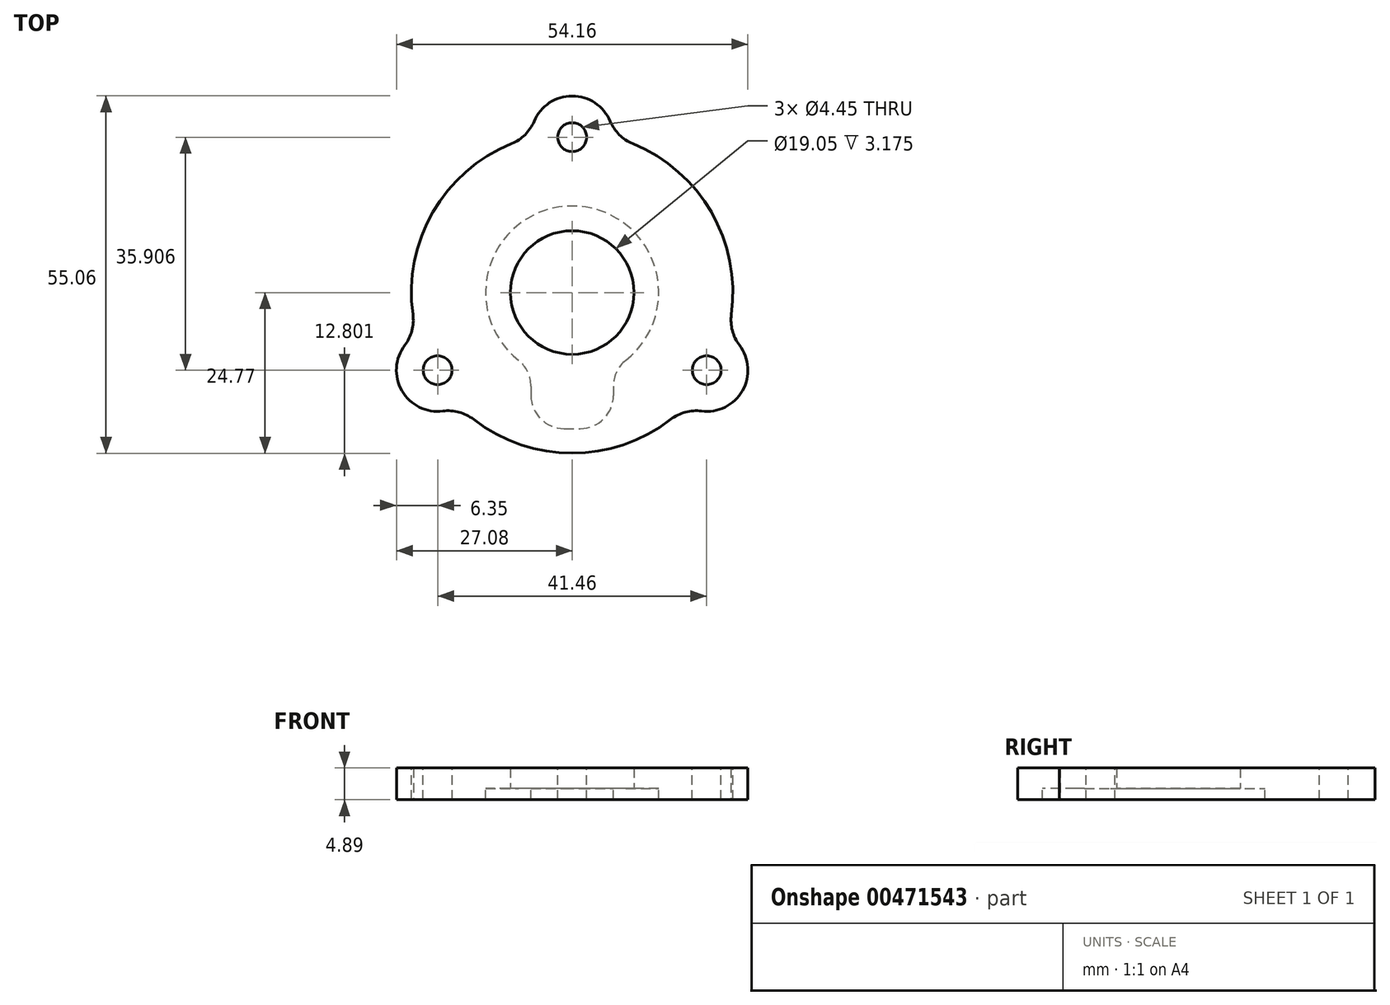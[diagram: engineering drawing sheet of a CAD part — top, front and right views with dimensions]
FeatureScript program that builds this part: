
annotation { "Feature Type Name" : "Feature", "Feature Type Description" : "" }
export const myFeature = defineFeature(function(context is Context, id is Id, definition is map)
    precondition{}
    {
        {
            var Q0;
            Q0=qCreatedBy(makeId("Top.planeOp"),FACE);
            var sketch = newSketch(context, id + "F0", { "sketchPlane" : qUnion([Q0])});
            skCircle(sketch, "E0", {"center": v(0, 0) * mm, "radius": 24.77 * mm});
            skLineSegment(sketch, "E1", {"start": v(0, 0) * mm, "end": v(0, 42.77) * mm, "construction": true});
            skLineSegment(sketch, "E2", {"start": v(0, 0) * mm, "end": v(-43.71, -25.24) * mm, "construction": true});
            skLineSegment(sketch, "E3", {"start": v(0, 0) * mm, "end": v(46.9, -27.08) * mm, "construction": true});
            skLineSegment(sketch, "E4", {"start": v(-6.35, 2.16) * mm, "end": v(-6.35, 48.97) * mm, "construction": true});
            skLineSegment(sketch, "E5.MirrorCS", {"start": v(6.35, 2.16) * mm, "end": v(6.35, 48.97) * mm, "construction": true});
            skLineSegment(sketch, "E6", {"start": v(-12.7, 0) * mm, "end": v(-48.99, -20.95) * mm, "construction": true});
            skLineSegment(sketch, "E7.MirrorCS", {"start": v(-6.35, -11) * mm, "end": v(-42.64, -31.95) * mm, "construction": true});
            skLineSegment(sketch, "E8", {"start": v(0.14, -7.41) * mm, "end": v(38.48, -29.55) * mm, "construction": true});
            skLineSegment(sketch, "E9.MirrorCS", {"start": v(6.49, 3.59) * mm, "end": v(44.83, -18.55) * mm, "construction": true});
            skArc(sketch, "E10", {"start": v(6.35, 23.94) * mm, "mid": v(0, 30.29) * mm, "end": v(-6.35, 23.94) * mm});
            skArc(sketch, "E11", {"start": v(-23.9, -6.47) * mm, "mid": v(-26.23, -15.14) * mm, "end": v(-17.56, -17.47) * mm});
            skArc(sketch, "E12", {"start": v(17.56, -17.47) * mm, "mid": v(26.23, -15.14) * mm, "end": v(23.9, -6.47) * mm});
            skCircle(sketch, "E13", {"center": v(0, 23.94) * mm, "radius": 2.22 * mm});
            skCircle(sketch, "E14", {"center": v(-20.73, -11.97) * mm, "radius": 2.22 * mm});
            skCircle(sketch, "E15", {"center": v(20.73, -11.97) * mm, "radius": 2.22 * mm});
            skCircle(sketch, "E16", {"center": v(0, 0) * mm, "radius": 9.53 * mm});
            skCircle(sketch, "E17", {"center": v(0, 0) * mm, "radius": 13.34 * mm});
            skLineSegment(sketch, "E18", {"start": v(-6.35, -11.73) * mm, "end": v(-6.35, -20.96) * mm});
            skLineSegment(sketch, "E19.MirrorCS", {"start": v(6.35, -11.73) * mm, "end": v(6.35, -20.96) * mm});
            skLineSegment(sketch, "E20", {"start": v(-6.35, -20.96) * mm, "end": v(6.35, -20.96) * mm});
            skSolve(sketch);
        }
        {
            var Q0;
            Q0 = qSketchRegion(id + "F0", true);
            extrude(context, id + "F1", {"entities" : qUnion([Q0]), "oppositeDirection" : true, "depth" : 1.71 * mm});
        }
        {
            var Q0;
            Q0=makeQuery(id+"F0.imprint","IMPRINT",FACE,{"disambiguationData":[TD([[makeQuery(id+"F0.imprint","IMPRINT",EDGE,{"derivedFrom":sQuery(id+"F0.wireOp",EDGE,"E16")}),-1.0]])]});
            var Q1;
            Q1=makeQuery(id+"F0.imprint","IMPRINT",FACE,{"disambiguationData":[TD([[makeQuery(id+"F0.imprint","IMPRINT",EDGE,{"derivedFrom":sQuery(id+"F0.wireOp",EDGE,"E17")}),-1.0]])]});
            var Q2;
            {var subQ0=sQuery(id+"F0.wireOp",EDGE,"E10");Q2=makeQuery(id+"F0.imprint","IMPRINT",FACE,{"disambiguationData":[TD([[makeQuery(id+"F0.imprint","IMPRINT",EDGE,{"derivedFrom":subQ0}),1.0]])]});}
            var Q3;
            {var subQ0=sQuery(id+"F0.wireOp",EDGE,"E11");Q3=makeQuery(id+"F0.imprint","IMPRINT",FACE,{"disambiguationData":[TD([[makeQuery(id+"F0.imprint","IMPRINT",EDGE,{"derivedFrom":subQ0}),1.0]])]});}
            var Q4;
            {var subQ0=sQuery(id+"F0.wireOp",EDGE,"E12");Q4=makeQuery(id+"F0.imprint","IMPRINT",FACE,{"disambiguationData":[TD([[makeQuery(id+"F0.imprint","IMPRINT",EDGE,{"derivedFrom":subQ0}),1.0]])]});}
            var Q5;
            {var subQ16=sQuery(id+"F0.wireOp",EDGE,"E18");Q5=makeQuery(id+"F0.imprint","IMPRINT",FACE,{"disambiguationData":[TD([[makeQuery(id+"F0.imprint","IMPRINT",EDGE,{"derivedFrom":subQ16}),-1.0]])]});}
            extrude(context, id + "F2", {"entities" : qUnion([Q0, Q1, Q2, Q3, Q4, Q5]), "operationType" : NewBodyOperationType.ADD, "depth" : 3.17 * mm});
        }
        {
            var Q0;
            {var subQ0=sQuery(id+"F0.wireOp",EDGE,"E11");var subQ1=sQuery(id+"F0.wireOp",EDGE,"E0");Q0=makeQuery(id+"F1.opExtrude","SWEPT_EDGE",EDGE,{"disambiguationData":[OSD([subQ1,subQ0]),TDD([makeQuery(id+"F0.imprint","INTERSECT",VERTEX,{"disambiguationData":[OD(1.0)],"derivedFrom":[subQ1,subQ0]})])]});}
            var Q1;
            {var subQ0=sQuery(id+"F0.wireOp",EDGE,"E11");var subQ1=sQuery(id+"F0.wireOp",EDGE,"E0");Q1=makeQuery(id+"F1.opExtrude","SWEPT_EDGE",EDGE,{"disambiguationData":[OSD([subQ1,subQ0]),TDD([makeQuery(id+"F0.imprint","INTERSECT",VERTEX,{"disambiguationData":[OD(0.0)],"derivedFrom":[subQ1,subQ0]})])]});}
            var Q2;
            {var subQ0=sQuery(id+"F0.wireOp",EDGE,"E10");var subQ1=sQuery(id+"F0.wireOp",EDGE,"E0");Q2=makeQuery(id+"F1.opExtrude","SWEPT_EDGE",EDGE,{"disambiguationData":[OSD([subQ1,subQ0]),TDD([makeQuery(id+"F0.imprint","INTERSECT",VERTEX,{"disambiguationData":[OD(1.0)],"derivedFrom":[subQ1,subQ0]})])]});}
            var Q3;
            {var subQ0=sQuery(id+"F0.wireOp",EDGE,"E10");var subQ1=sQuery(id+"F0.wireOp",EDGE,"E0");Q3=makeQuery(id+"F1.opExtrude","SWEPT_EDGE",EDGE,{"disambiguationData":[OSD([subQ1,subQ0]),TDD([makeQuery(id+"F0.imprint","INTERSECT",VERTEX,{"disambiguationData":[OD(0.0)],"derivedFrom":[subQ1,subQ0]})])]});}
            var Q4;
            {var subQ0=sQuery(id+"F0.wireOp",EDGE,"E12");var subQ1=sQuery(id+"F0.wireOp",EDGE,"E0");Q4=makeQuery(id+"F1.opExtrude","SWEPT_EDGE",EDGE,{"disambiguationData":[OSD([subQ1,subQ0]),TDD([makeQuery(id+"F0.imprint","INTERSECT",VERTEX,{"disambiguationData":[OD(1.0)],"derivedFrom":[subQ1,subQ0]})])]});}
            var Q5;
            {var subQ0=sQuery(id+"F0.wireOp",EDGE,"E12");var subQ1=sQuery(id+"F0.wireOp",EDGE,"E0");Q5=makeQuery(id+"F1.opExtrude","SWEPT_EDGE",EDGE,{"disambiguationData":[OSD([subQ1,subQ0]),TDD([makeQuery(id+"F0.imprint","INTERSECT",VERTEX,{"disambiguationData":[OD(0.0)],"derivedFrom":[subQ1,subQ0]})])]});}
            fillet(context, id + "F3", {"entities" : qUnion([Q0, Q1, Q2, Q3, Q4, Q5]), "radius" : 6.35 * mm, "tangentPropagation" : true, "allowEdgeOverflow" : false});
        }
        {
            var Q0;
            Q0=makeQuery(id+"F1.opExtrude","SWEPT_EDGE",EDGE,{"disambiguationData":[OSD([sQuery(id+"F0.wireOp",EDGE,"E17"),sQuery(id+"F0.wireOp",EDGE,"E18")])]});
            var Q1;
            Q1=makeQuery(id+"F1.opExtrude","SWEPT_EDGE",EDGE,{"disambiguationData":[OSD([sQuery(id+"F0.wireOp",EDGE,"E17"),sQuery(id+"F0.wireOp",EDGE,"E19.MirrorCS")])]});
            var Q2;
            Q2=makeQuery(id+"F1.opExtrude","SWEPT_EDGE",EDGE,{"disambiguationData":[OSD([sQuery(id+"F0.wireOp",EDGE,"E19.MirrorCS"),sQuery(id+"F0.wireOp",EDGE,"E20")])]});
            var Q3;
            Q3=makeQuery(id+"F1.opExtrude","SWEPT_EDGE",EDGE,{"disambiguationData":[OSD([sQuery(id+"F0.wireOp",EDGE,"E18"),sQuery(id+"F0.wireOp",EDGE,"E20")])]});
            fillet(context, id + "F4", {"entities" : qUnion([Q0, Q1, Q2, Q3]), "radius" : 5.08 * mm, "tangentPropagation" : true, "allowEdgeOverflow" : false});
        }
    });
